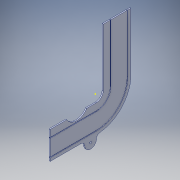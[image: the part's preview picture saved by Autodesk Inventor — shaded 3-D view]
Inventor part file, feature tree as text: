
AUTODESK INVENTOR PART (.ipt)
format: ipt  version: 2016 (Build 200138000, 138)  size: 151,552 bytes
history: native  units: in
note: dims shown in document units (in); Inventor stores cm internally (conversion verified against a paired STEP export)
features: sketch x1, other x1
ambient origin geometry x8: Origin, YZ Plane, XZ Plane, XY Plane, X Axis, Y Axis, Z Axis, Center Point
bodies: Solid1 (feature_tree)
feature tree (2):
  sketch  "Sketch1"
  other  "Cut-Extrude3"
